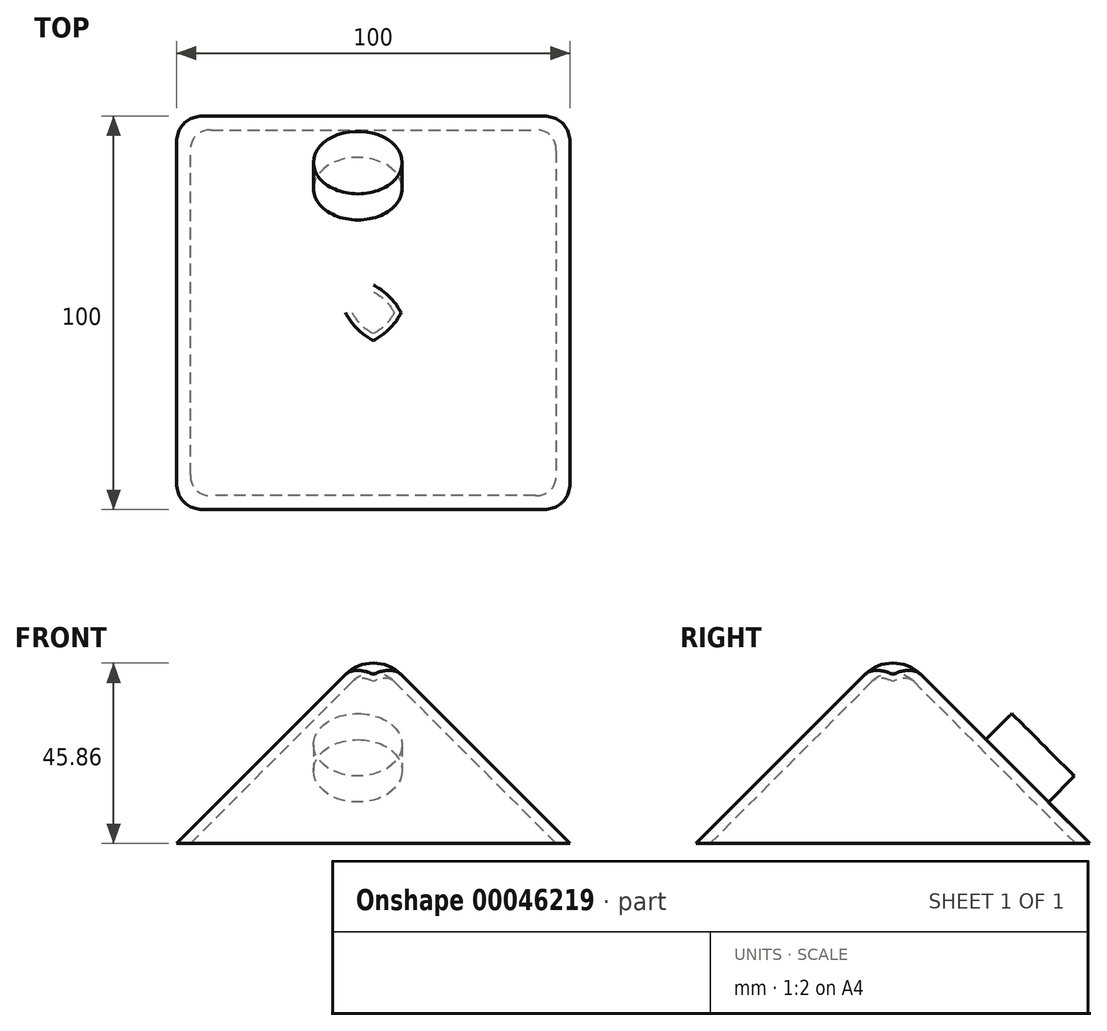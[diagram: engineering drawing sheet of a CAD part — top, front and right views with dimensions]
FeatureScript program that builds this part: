
annotation { "Feature Type Name" : "Feature", "Feature Type Description" : "" }
export const myFeature = defineFeature(function(context is Context, id is Id, definition is map)
    precondition{}
    {
        {
            var Q0;
            Q0=qCreatedBy(makeId("Top.planeOp"),FACE);
            var sketch = newSketch(context, id + "F0", { "sketchPlane" : qUnion([Q0])});
            skLineSegment(sketch, "E0.rect.bottom", {"start": v(-50, 50) * mm, "end": v(50, 50) * mm});
            skLineSegment(sketch, "E0.rect.top", {"start": v(-50, -50) * mm, "end": v(50, -50) * mm});
            skLineSegment(sketch, "E0.rect.left", {"start": v(-50, 50) * mm, "end": v(-50, -50) * mm});
            skLineSegment(sketch, "E0.rect.right", {"start": v(50, 50) * mm, "end": v(50, -50) * mm});
            skPoint(sketch, "E0.rect.middle", {"position": v(0, 0) * mm});
            skSolve(sketch);
        }
        {
            var Q0;
            Q0=makeQuery(id+"F0.imprint","IMPRINT",FACE,{"disambiguationData":[TD([[makeQuery(id+"F0.imprint","IMPRINT",EDGE,{"derivedFrom":sQuery(id+"F0.wireOp",EDGE,"E0.rect.bottom")}),-1.0]])]});
            extrude(context, id + "F1", {"entities" : qUnion([Q0]), "depth" : 50 * mm, "hasDraft" : true, "draftAngle" : 45 * degree, "draftPullDirection" : true});
        }
        {
            var Q0;
            Q0=makeQuery(id+"F1.opExtrude","SWEPT_EDGE",EDGE,{"disambiguationData":[OSD([sQuery(id+"F0.wireOp",EDGE,"E0.rect.top"),sQuery(id+"F0.wireOp",EDGE,"E0.rect.left")])]});
            var Q1;
            Q1=makeQuery(id+"F1.opExtrude","SWEPT_EDGE",EDGE,{"disambiguationData":[OSD([sQuery(id+"F0.wireOp",EDGE,"E0.rect.bottom"),sQuery(id+"F0.wireOp",EDGE,"E0.rect.left")])]});
            var Q2;
            Q2=makeQuery(id+"F1.opExtrude","SWEPT_EDGE",EDGE,{"disambiguationData":[OSD([sQuery(id+"F0.wireOp",EDGE,"E0.rect.top"),sQuery(id+"F0.wireOp",EDGE,"E0.rect.right")])]});
            var Q3;
            Q3=makeQuery(id+"F1.opExtrude","SWEPT_EDGE",EDGE,{"disambiguationData":[OSD([sQuery(id+"F0.wireOp",EDGE,"E0.rect.bottom"),sQuery(id+"F0.wireOp",EDGE,"E0.rect.right")])]});
            fillet(context, id + "F2", {"entities" : qUnion([Q0, Q1, Q2, Q3]), "radius" : 10 * mm, "tangentPropagation" : true, "allowEdgeOverflow" : false});
        }
        {
            var Q0;
            Q0=makeQuery(id+"F1.opExtrude","CAP_FACE",FACE,{"disambiguationData":[OSD([sQuery(id+"F0.wireOp",EDGE,"E0.rect.bottom"),sQuery(id+"F0.wireOp",EDGE,"E0.rect.top"),sQuery(id+"F0.wireOp",EDGE,"E0.rect.left"),sQuery(id+"F0.wireOp",EDGE,"E0.rect.right")])],"isStart":true});
            shell(context, id + "F3", {"entities" : qUnion([Q0]), "thickness" : 2.5 * mm});
        }
        {
            var Q0;
            {var subQ0=sQuery(id+"F0.wireOp",EDGE,"E0.rect.bottom");Q0=makeQuery(id+"F1.draft0.opDraft","MERGE",FACE,{"derivedFrom":[makeQuery(id+"F1.opExtrude","SWEPT_FACE",FACE,{"disambiguationData":[OSD([subQ0])]}),makeQuery(id+"F1.opExtrude","CAP_FACE",FACE,{"disambiguationData":[OSD([subQ0,sQuery(id+"F0.wireOp",EDGE,"E0.rect.top"),sQuery(id+"F0.wireOp",EDGE,"E0.rect.left"),sQuery(id+"F0.wireOp",EDGE,"E0.rect.right")])],"isStart":false})]});}
            var sketch = newSketch(context, id + "F4", { "sketchPlane" : qUnion([Q0])});
            skCircle(sketch, "E1", {"center": v(3.93, -9.25) * mm, "radius": 11.24 * mm});
            skSolve(sketch);
        }
        {
            var Q0;
            Q0=makeQuery(id+"F4.imprint","IMPRINT",FACE,{"disambiguationData":[TD([[makeQuery(id+"F4.imprint","IMPRINT",EDGE,{"derivedFrom":sQuery(id+"F4.wireOp",EDGE,"E1")}),1.0]])]});
            extrude(context, id + "F5", {"entities" : qUnion([Q0]), "operationType" : NewBodyOperationType.ADD, "depth" : 9.36 * mm});
        }
    });
